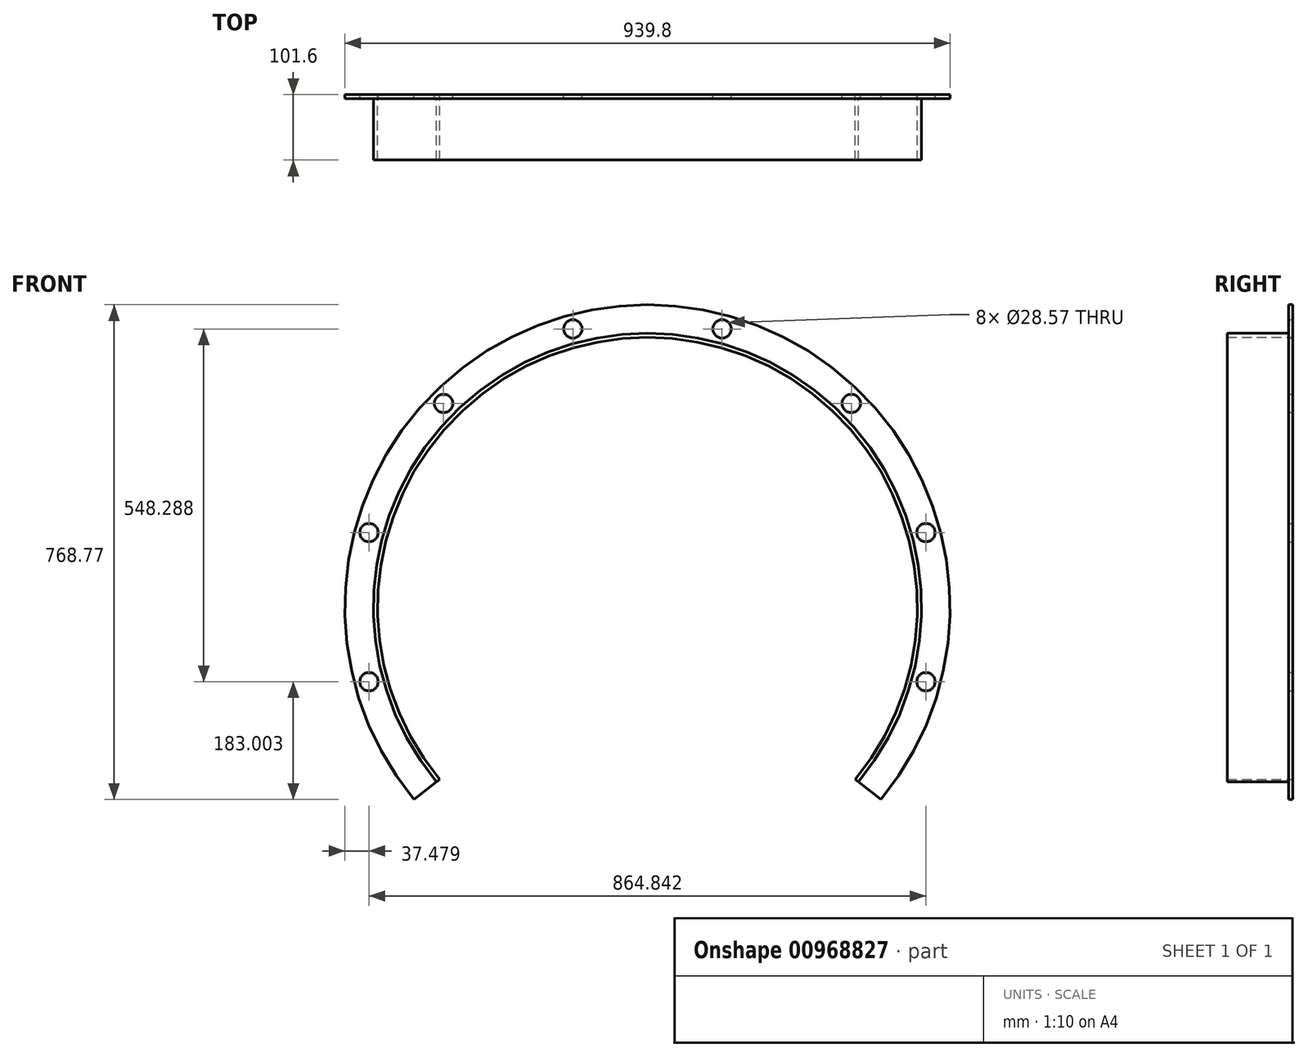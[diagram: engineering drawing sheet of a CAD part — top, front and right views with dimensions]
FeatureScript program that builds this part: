
annotation { "Feature Type Name" : "Feature", "Feature Type Description" : "" }
export const myFeature = defineFeature(function(context is Context, id is Id, definition is map)
    precondition{}
    {
        {
            var Q0;
            Q0=qCreatedBy(makeId("Front.planeOp"),FACE);
            var sketch = newSketch(context, id + "F0", { "sketchPlane" : qUnion([Q0])});
            skArc(sketch, "E0", {"start": v(362.6, -298.87) * mm, "mid": v(0, 469.9) * mm, "end": v(-362.6, -298.87) * mm});
            skArc(sketch, "E1.0", {"start": v(327.58, -271.48) * mm, "mid": v(0, 425.45) * mm, "end": v(-327.58, -271.48) * mm});
            skArc(sketch, "E2.0", {"start": v(306.3, -326.5) * mm, "mid": v(316.55, -316.55) * mm, "end": v(326.5, -306.3) * mm, "construction": true});
            skArc(sketch, "E3.0", {"start": v(322.58, -267.56) * mm, "mid": v(0, 419.1) * mm, "end": v(-322.58, -267.56) * mm});
            skArc(sketch, "E4", {"start": v(250.83, 0) * mm, "mid": v(0, 250.83) * mm, "end": v(-250.83, 0) * mm});
            skLineSegment(sketch, "E5", {"start": v(0, 447.68) * mm, "end": v(0, 0) * mm, "construction": true});
            skLineSegment(sketch, "E6", {"start": v(0, 0) * mm, "end": v(115.87, 432.42) * mm, "construction": true});
            skPoint(sketch, "E7", {"position": v(115.87, 432.42) * mm});
            skCircle(sketch, "E8", {"center": v(115.87, 432.42) * mm, "radius": 14.29 * mm});
            skCircle(sketch, "E9.1.0", {"center": v(-115.87, 432.42) * mm, "radius": 14.29 * mm});
            skCircle(sketch, "E9.2.0", {"center": v(-316.55, 316.55) * mm, "radius": 14.29 * mm});
            skCircle(sketch, "E9.3.0", {"center": v(-432.42, 115.87) * mm, "radius": 14.29 * mm});
            skCircle(sketch, "E9.4.0", {"center": v(-432.42, -115.87) * mm, "radius": 14.29 * mm});
            skCircle(sketch, "E9.5.0", {"center": v(-316.55, -316.55) * mm, "radius": 14.29 * mm});
            skCircle(sketch, "E9.6.0", {"center": v(-115.87, -432.42) * mm, "radius": 14.29 * mm});
            skCircle(sketch, "E9.7.0", {"center": v(115.87, -432.42) * mm, "radius": 14.29 * mm});
            skArc(sketch, "E9.8.0", {"start": v(326.5, -306.3) * mm, "mid": v(306.45, -306.45) * mm, "end": v(306.3, -326.5) * mm});
            skCircle(sketch, "E9.9.0", {"center": v(432.42, -115.87) * mm, "radius": 14.29 * mm});
            skCircle(sketch, "E9.10.0", {"center": v(432.42, 115.87) * mm, "radius": 14.29 * mm});
            skCircle(sketch, "E9.11.0", {"center": v(316.55, 316.55) * mm, "radius": 14.29 * mm});
            skPoint(sketch, "E10", {"position": v(345.1, -285.17) * mm});
            skLineSegment(sketch, "E11", {"start": v(250.83, 0) * mm, "end": v(250.83, -168.12) * mm});
            skLineSegment(sketch, "E12", {"start": v(284.96, -238.15) * mm, "end": v(362.6, -298.87) * mm});
            skPoint(sketch, "E13.newPointA", {"position": v(247.56, -208.9) * mm});
            skArc(sketch, "E13.filletArc", {"start": v(250.83, -168.12) * mm, "mid": v(259.81, -207.08) * mm, "end": v(284.96, -238.15) * mm});
            skLineSegment(sketch, "E14.MirrorCS", {"start": v(-250.83, 0) * mm, "end": v(-250.83, -168.12) * mm});
            skArc(sketch, "E15.MirrorCS", {"start": v(-250.83, -168.12) * mm, "mid": v(-259.81, -207.08) * mm, "end": v(-284.96, -238.15) * mm});
            skLineSegment(sketch, "E16.MirrorCS", {"start": v(-284.96, -238.15) * mm, "end": v(-362.6, -298.87) * mm});
            skLineSegment(sketch, "E17", {"start": v(247.56, -208.9) * mm, "end": v(247.56, -399.4) * mm, "construction": true});
            skArc(sketch, "E18.trimOffspring", {"start": v(345.1, -285.17) * mm, "mid": v(0, 447.68) * mm, "end": v(-345.1, -285.17) * mm, "construction": true});
            skArc(sketch, "E19.trimOffspring", {"start": v(-326.5, -306.3) * mm, "mid": v(-316.55, -316.55) * mm, "end": v(-306.3, -326.5) * mm, "construction": true});
            skArc(sketch, "E20.trimOffspring", {"start": v(-129.6, -428.5) * mm, "mid": v(-115.87, -432.42) * mm, "end": v(-102, -435.9) * mm, "construction": true});
            skArc(sketch, "E21.trimOffspring", {"start": v(102, -435.9) * mm, "mid": v(115.87, -432.42) * mm, "end": v(129.6, -428.5) * mm, "construction": true});
            skSolve(sketch);
        }
        {
            var Q0;
            {var subQ0=sQuery(id+"F0.wireOp",EDGE,"E0");Q0=makeQuery(id+"F0.imprint","IMPRINT",FACE,{"disambiguationData":[TD([[makeQuery(id+"F0.imprint","IMPRINT",EDGE,{"derivedFrom":subQ0}),1.0]])]});}
            extrude(context, id + "F1", {"entities" : qUnion([Q0]), "depth" : 6.35 * mm, "offsetDistance" : 25.4 * mm});
        }
        {
            var Q0;
            {var subQ0=sQuery(id+"F0.wireOp",EDGE,"E1.0");Q0=makeQuery(id+"F0.imprint","IMPRINT",FACE,{"disambiguationData":[TD([[makeQuery(id+"F0.imprint","IMPRINT",EDGE,{"derivedFrom":subQ0}),1.0]])]});}
            extrude(context, id + "F2", {"entities" : qUnion([Q0]), "operationType" : NewBodyOperationType.ADD, "depth" : 101.6 * mm, "offsetDistance" : 25.4 * mm});
        }
    });
